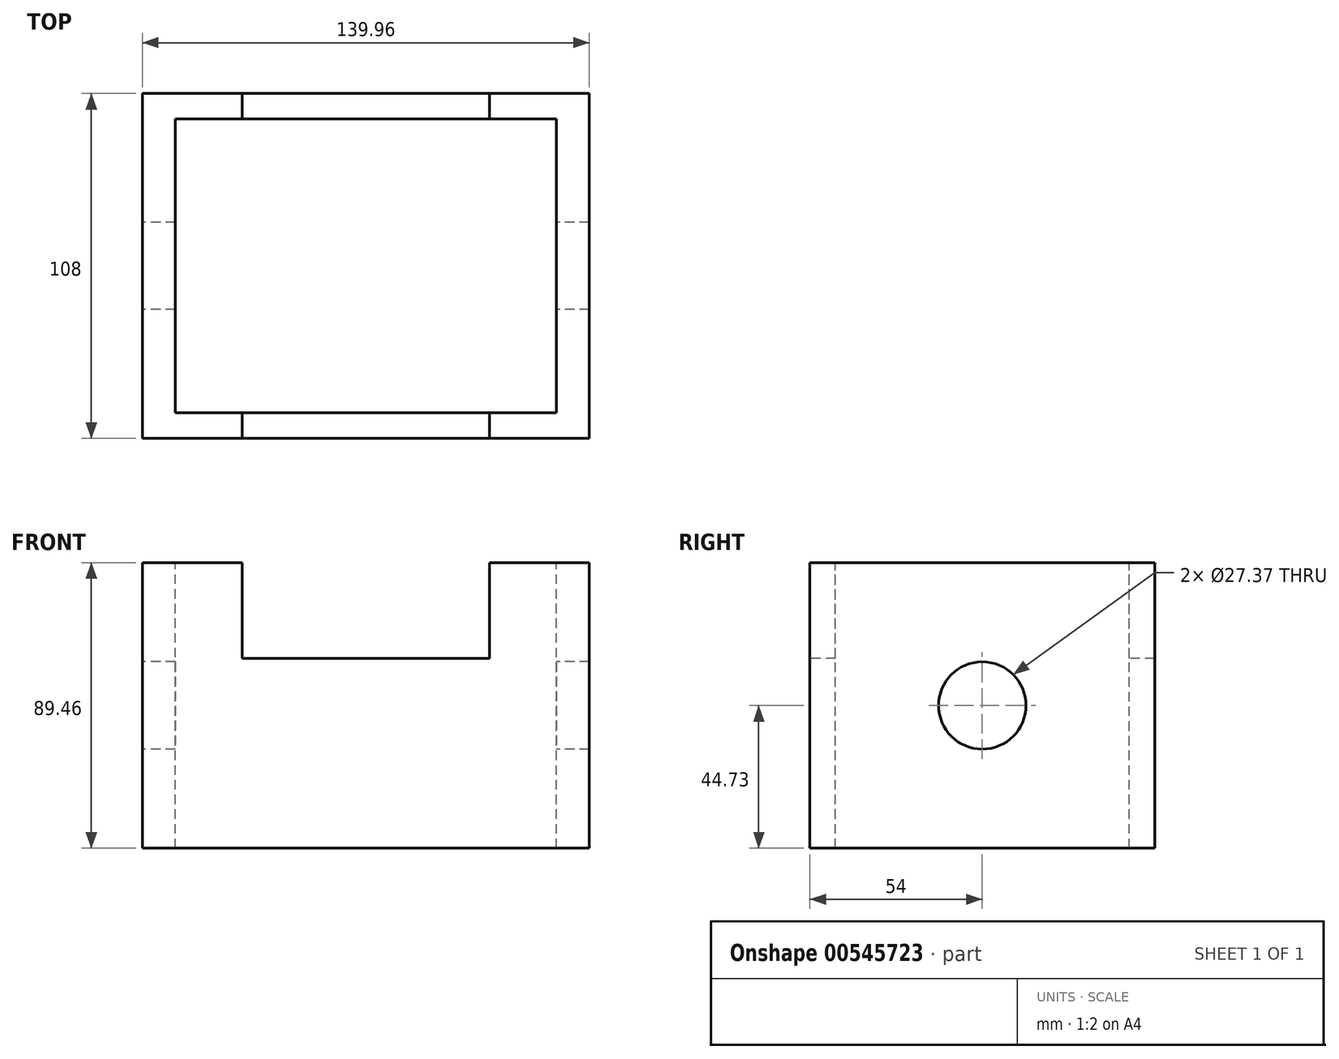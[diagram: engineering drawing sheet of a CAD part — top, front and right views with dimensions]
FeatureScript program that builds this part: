
annotation { "Feature Type Name" : "Feature", "Feature Type Description" : "" }
export const myFeature = defineFeature(function(context is Context, id is Id, definition is map)
    precondition{}
    {
        {
            var Q0;
            Q0=qCreatedBy(makeId("Front.planeOp"),FACE);
            var sketch = newSketch(context, id + "F0", { "sketchPlane" : qUnion([Q0])});
            skLineSegment(sketch, "E0.bottom", {"start": v(69.98, 44.73) * mm, "end": v(-69.98, 44.73) * mm});
            skLineSegment(sketch, "E0.top", {"start": v(69.98, -44.73) * mm, "end": v(-69.98, -44.73) * mm});
            skLineSegment(sketch, "E0.left", {"start": v(69.98, 44.73) * mm, "end": v(69.98, -44.73) * mm});
            skLineSegment(sketch, "E0.right", {"start": v(-69.98, 44.73) * mm, "end": v(-69.98, -44.73) * mm});
            skPoint(sketch, "E0.middle", {"position": v(0, 0) * mm});
            skSolve(sketch);
        }
        {
            var Q0;
            Q0 = qSketchRegion(id + "F0", true);
            extrude(context, id + "F1", {"entities" : qUnion([Q0]), "depth" : 54 * mm, "offsetDistance" : 25 * mm});
        }
        {
            var Q0;
            Q0=makeQuery(id+"F1.opExtrude","SWEPT_BODY",BODY,{"disambiguationData":[OSD([sQuery(id+"F0.wireOp",EDGE,"E0.bottom"),sQuery(id+"F0.wireOp",EDGE,"E0.top"),sQuery(id+"F0.wireOp",EDGE,"E0.left"),sQuery(id+"F0.wireOp",EDGE,"E0.right")])]});
            var Q1;
            Q1=makeQuery(id+"F1.opExtrude","CAP_FACE",FACE,{"disambiguationData":[OSD([sQuery(id+"F0.wireOp",EDGE,"E0.bottom"),sQuery(id+"F0.wireOp",EDGE,"E0.top"),sQuery(id+"F0.wireOp",EDGE,"E0.left"),sQuery(id+"F0.wireOp",EDGE,"E0.right")])],"isStart":true});
            mirror(context, id + "F2", {"operationType" : NewBodyOperationType.ADD, "entities" : qUnion([Q0]), "mirrorPlane" : qUnion([Q1])});
        }
        {
            var Q0;
            {var subQ0=makeQuery(id+"F1.opExtrude","SWEPT_FACE",FACE,{"disambiguationData":[OSD([sQuery(id+"F0.wireOp",EDGE,"E0.bottom")])]});Q0=makeQuery(id+"F2.boolean.opBoolean","MERGE",FACE,{"derivedFrom":[subQ0,makeQuery(id+"F2.opPattern","COPY",FACE,{"derivedFrom":subQ0,"instanceName":"1"})]});}
            var sketch = newSketch(context, id + "F3", { "sketchPlane" : qUnion([Q0])});
            skLineSegment(sketch, "E1.bottom", {"start": v(59.7, 46.01) * mm, "end": v(-59.7, 46.01) * mm});
            skLineSegment(sketch, "E1.top", {"start": v(59.7, -46.01) * mm, "end": v(-59.7, -46.01) * mm});
            skLineSegment(sketch, "E1.left", {"start": v(59.7, 46.01) * mm, "end": v(59.7, -46.01) * mm});
            skLineSegment(sketch, "E1.right", {"start": v(-59.7, 46.01) * mm, "end": v(-59.7, -46.01) * mm});
            skPoint(sketch, "E1.middle", {"position": v(0, 0) * mm});
            skSolve(sketch);
        }
        {
            var Q0;
            Q0 = qSketchRegion(id + "F3", true);
            extrude(context, id + "F4", {"entities" : qUnion([Q0]), "operationType" : NewBodyOperationType.REMOVE, "oppositeDirection" : true, "depth" : 98 * mm, "offsetDistance" : 25 * mm});
        }
        {
            var Q0;
            Q0=makeQuery(id+"F1.opExtrude","CAP_FACE",FACE,{"disambiguationData":[OSD([sQuery(id+"F0.wireOp",EDGE,"E0.bottom"),sQuery(id+"F0.wireOp",EDGE,"E0.top"),sQuery(id+"F0.wireOp",EDGE,"E0.left"),sQuery(id+"F0.wireOp",EDGE,"E0.right")])],"isStart":false});
            var sketch = newSketch(context, id + "F5", { "sketchPlane" : qUnion([Q0])});
            skLineSegment(sketch, "E2.left", {"start": v(-38.74, 44.73) * mm, "end": v(-38.74, 14.77) * mm});
            skLineSegment(sketch, "E3.right", {"start": v(38.74, 44.73) * mm, "end": v(38.74, 14.77) * mm});
            skPoint(sketch, "E2.right.end.orphan", {"position": v(0, 14.77) * mm});
            skLineSegment(sketch, "E4", {"start": v(-38.74, 44.73) * mm, "end": v(38.74, 44.73) * mm});
            skLineSegment(sketch, "E5", {"start": v(-38.74, 14.77) * mm, "end": v(38.74, 14.77) * mm});
            skSolve(sketch);
        }
        {
            var Q0;
            Q0 = qSketchRegion(id + "F5", true);
            extrude(context, id + "F6", {"entities" : qUnion([Q0]), "operationType" : NewBodyOperationType.REMOVE, "oppositeDirection" : true, "depth" : 195 * mm, "offsetDistance" : 25 * mm});
        }
        {
            var Q0;
            {var subQ0=makeQuery(id+"F1.opExtrude","SWEPT_FACE",FACE,{"disambiguationData":[OSD([sQuery(id+"F0.wireOp",EDGE,"E0.right")])]});Q0=makeQuery(id+"F2.boolean.opBoolean","MERGE",FACE,{"derivedFrom":[subQ0,makeQuery(id+"F2.opPattern","COPY",FACE,{"derivedFrom":subQ0,"instanceName":"1"})]});}
            var sketch = newSketch(context, id + "F7", { "sketchPlane" : qUnion([Q0])});
            skCircle(sketch, "E6", {"center": v(0, 0) * mm, "radius": 13.69 * mm});
            skSolve(sketch);
        }
        {
            var Q0;
            Q0 = qSketchRegion(id + "F7", true);
            extrude(context, id + "F8", {"entities" : qUnion([Q0]), "operationType" : NewBodyOperationType.REMOVE, "oppositeDirection" : true, "depth" : 202 * mm, "offsetDistance" : 25 * mm});
        }
    });
